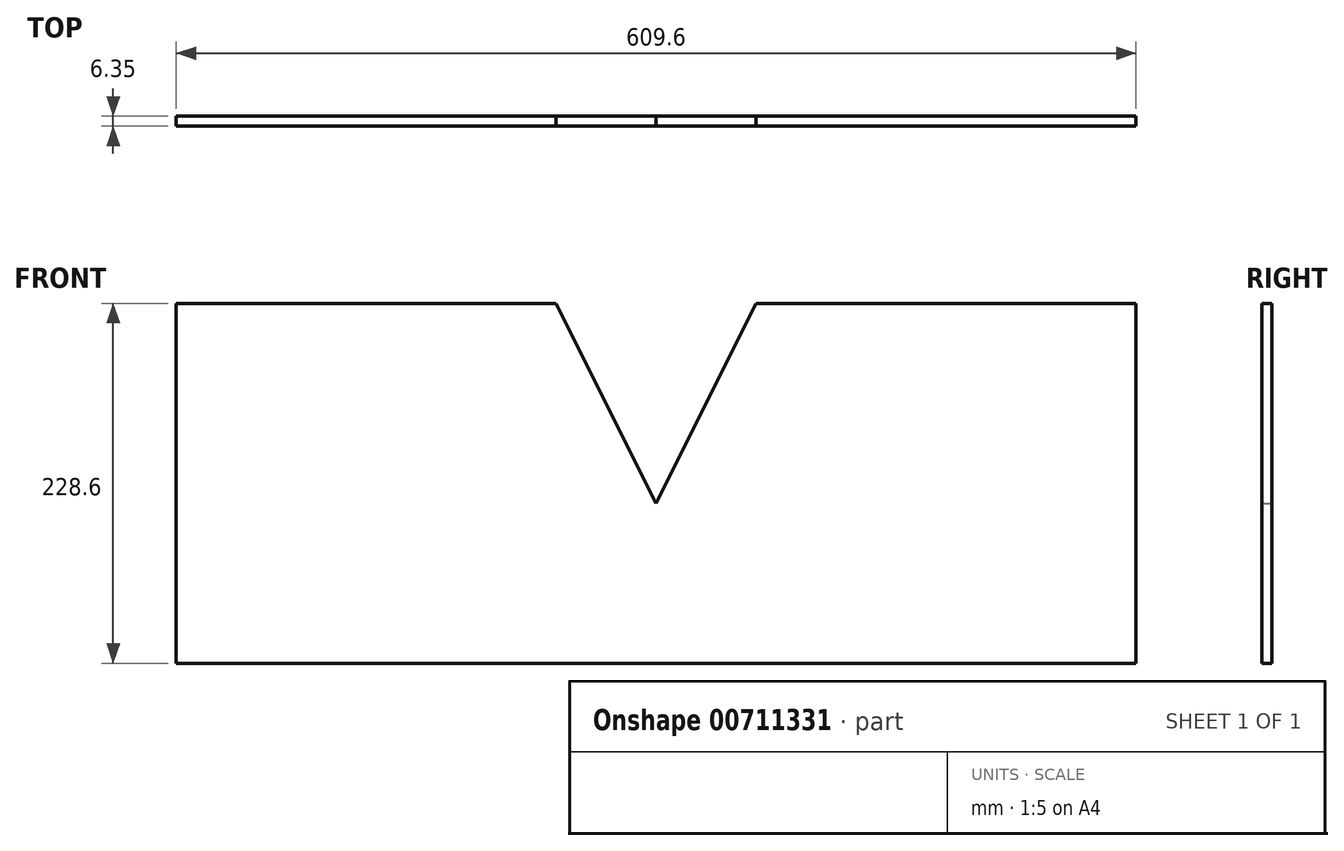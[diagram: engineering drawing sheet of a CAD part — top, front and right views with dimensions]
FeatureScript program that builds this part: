
annotation { "Feature Type Name" : "Feature", "Feature Type Description" : "" }
export const myFeature = defineFeature(function(context is Context, id is Id, definition is map)
    precondition{}
    {
        {
            var Q0;
            Q0=qCreatedBy(makeId("Front.planeOp"),FACE);
            var sketch = newSketch(context, id + "F0", { "sketchPlane" : qUnion([Q0])});
            skLineSegment(sketch, "E0.bottom", {"start": v(88.9, 114.3) * mm, "end": v(-152.4, 114.3) * mm});
            skLineSegment(sketch, "E0.top", {"start": v(152.4, -114.3) * mm, "end": v(-152.4, -114.3) * mm});
            skLineSegment(sketch, "E0.left", {"start": v(152.4, -12.7) * mm, "end": v(152.4, -114.3) * mm});
            skLineSegment(sketch, "E0.right", {"start": v(-152.4, 114.3) * mm, "end": v(-152.4, -114.3) * mm});
            skPoint(sketch, "E0.middle", {"position": v(0, 0) * mm});
            skLineSegment(sketch, "E1", {"start": v(88.9, 114.3) * mm, "end": v(152.4, -12.7) * mm});
            skPoint(sketch, "E2.orphan", {"position": v(152.4, 114.3) * mm});
            skLineSegment(sketch, "E3.MirrorCS", {"start": v(215.9, 114.3) * mm, "end": v(457.2, 114.3) * mm});
            skLineSegment(sketch, "E4.MirrorCS", {"start": v(152.4, -114.3) * mm, "end": v(457.2, -114.3) * mm});
            skLineSegment(sketch, "E5.MirrorCS", {"start": v(457.2, 114.3) * mm, "end": v(457.2, -114.3) * mm});
            skLineSegment(sketch, "E6.MirrorCS", {"start": v(215.9, 114.3) * mm, "end": v(152.4, -12.7) * mm});
            skPoint(sketch, "E7.MirrorP", {"position": v(304.8, 0) * mm});
            skSolve(sketch);
        }
        {
            var Q0;
            Q0 = qSketchRegion(id + "F0", true);
            extrude(context, id + "F1", {"entities" : qUnion([Q0]), "depth" : 6.35 * mm, "offsetDistance" : 25.4 * mm});
        }
    });
